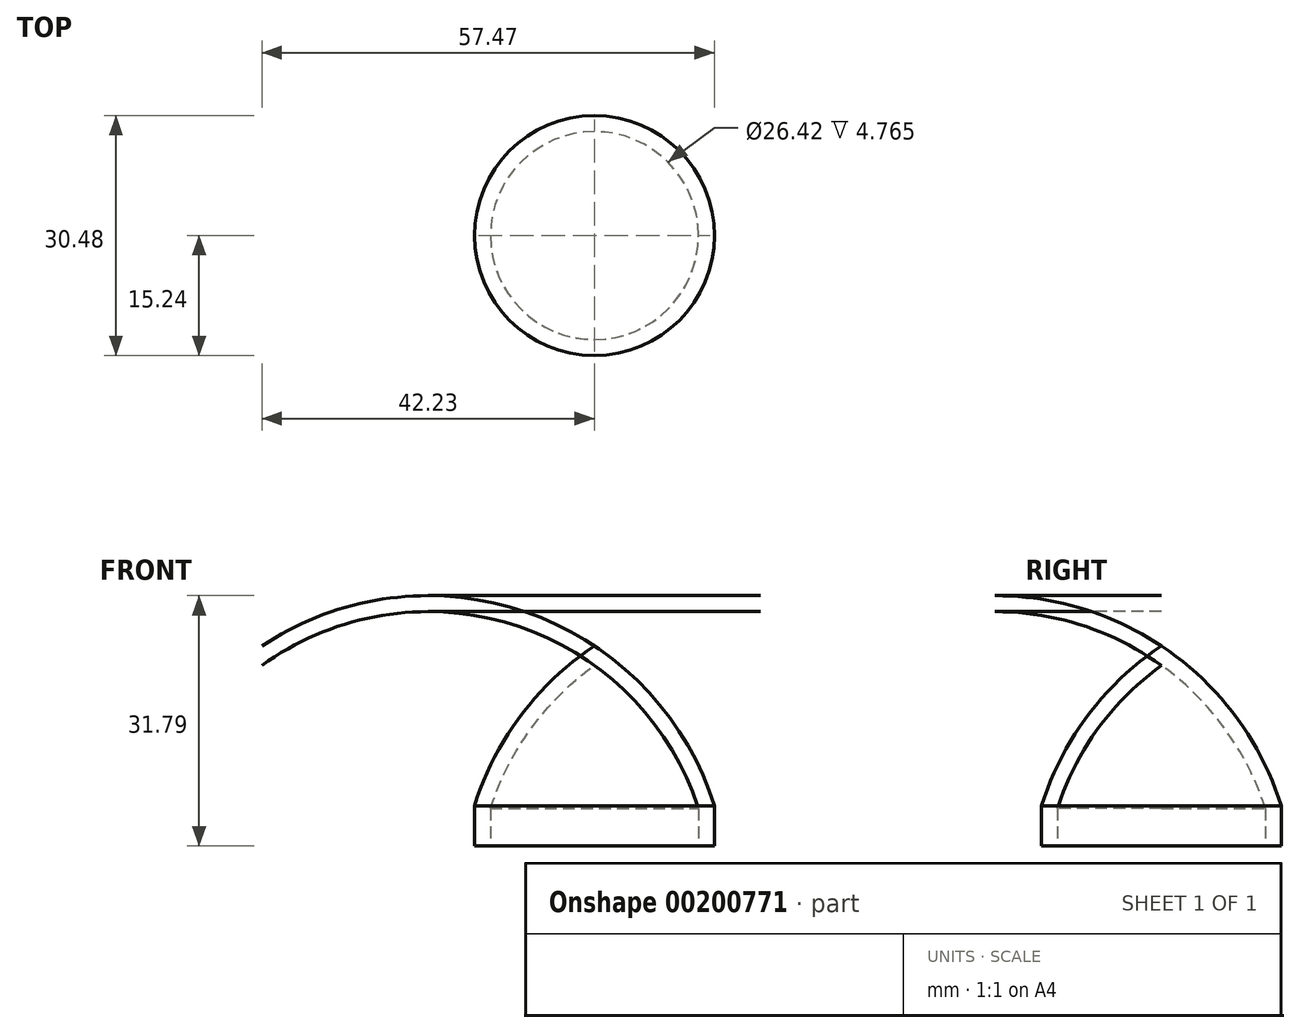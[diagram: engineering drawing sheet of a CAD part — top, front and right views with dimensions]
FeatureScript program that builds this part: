
annotation { "Feature Type Name" : "Feature", "Feature Type Description" : "" }
export const myFeature = defineFeature(function(context is Context, id is Id, definition is map)
    precondition{}
    {
        {
            var Q0;
            Q0=qCreatedBy(makeId("Front.planeOp"),FACE);
            var sketch = newSketch(context, id + "F0", { "sketchPlane" : qUnion([Q0])});
            skLineSegment(sketch, "E0", {"start": v(0, 0) * mm, "end": v(-15.24, 0) * mm});
            skLineSegment(sketch, "E1", {"start": v(-15.24, 0) * mm, "end": v(-15.24, 5.08) * mm});
            skLineSegment(sketch, "E2", {"start": v(0, 0) * mm, "end": v(0, 25.4) * mm});
            skArc(sketch, "E3", {"start": v(0, 25.4) * mm, "mid": v(-9.36, 16.55) * mm, "end": v(-15.24, 5.08) * mm});
            skSolve(sketch);
        }
        {
            var Q0;
            Q0=makeQuery(id+"F0.imprint","IMPRINT",FACE,{"disambiguationData":[TD([[makeQuery(id+"F0.imprint","IMPRINT",EDGE,{"derivedFrom":sQuery(id+"F0.wireOp",EDGE,"E0")}),-1.0]])]});
            var Q1;
            Q1=sQuery(id+"F0.wireOp",EDGE,"E2");
            revolve(context, id + "F1", {"entities" : qUnion([Q0]), "axis" : qUnion([Q1]), "revolveType" : RevolveType.FULL});
        }
        {
            var Q0;
            Q0=makeQuery(id+"F1.opRevolve","SWEPT_FACE",FACE,{"disambiguationData":[OSD([sQuery(id+"F0.wireOp",EDGE,"E0")])]});
            shell(context, id + "F2", {"entities" : qUnion([Q0]), "thickness" : 2.03 * mm});
        }
    });
